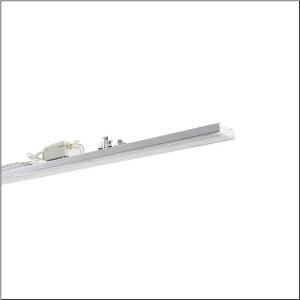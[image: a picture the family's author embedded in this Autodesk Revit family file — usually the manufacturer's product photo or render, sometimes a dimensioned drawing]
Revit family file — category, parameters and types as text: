
# Revit family: licross_11_recessed_ho_51tl12cn4c5m
name_source: partatom
category: Lighting Fixtures
units: mm (PartAtom-declared; Revit-internal decimal feet)

## family parameters
Cut with Voids When Loaded = No
Host = Face
Light Source = No
Part Type = Normal
Room Calculation Point = No
Round Connector Dimension = Use Diameter
Shared = No

## types (1)
- --- (1 x LED, 12740 lm, 66.5 W, 4000K)
    Apparent Load = 67 VA
    CIE Flux Codes = 66 91 98 100 100
    Color Rendering = 80
    Color Temperature = 4000K
    Default Elevation = 1800 mm
    Description = Licross 11 Recessed HO, luminaire insert, of sheet steel, coil coated, white, length: 1.500mm, width: 66mm, height: 67mm, LED rated luminous flux: 12.740lm, light colour: 840, SDCM (Standard Deviation of Colour Matching)MacAdam ≤ 2 SDCM (initial), control gear: ON/OFF Multilumen, CLOi, with plug, 3-pole, with phase selection, mains connection: 220..240V, AC, 50/60Hz, start of lifetime: 67W, end of service life: 75W, internal wiring halogen-free, primary optical cover: cover, of PMMA, light emission: direct distribution, primary light characteristic: symmetric, protection rating (complete): IP40, insulation class (complete): insulation class I (protective earthing), certification: CE, ENEC, VDE, UKCA, protection symbol: D if used in an environment without relevant dust loads with corresponding accessories, impact resistance: IK06, permissible ambient temperature for indoor applications: -35..+35°C, corresponds to IFS (International Featured Standards) requirements for safety and quality in the food industry, reducing of maximum allowable ambient temperature of 5°C with ceiling mounting, LABS conformity tested according to VDMA 24364:2018-05, The light source and the operating device comply with the requirements of the Ecodesign Regulation (EU) 2019/2020 and are replaceable in accordance with this regulation, packaging unit: 1 piece
    Height = 58 mm
    Lamp = 1 x LED
    Lamp Light Flux = 12740 lm
    Lamp Power = 66.5 W
    Lamp count = 1
    Length = 1500 mm
    Luminous efficacy = 192 lm/W
    Manufacturer = Siteco
    ModVariant = No
    Model = 51TL12CN4C5M
    Mounting Place = Ceiling
    Mounting Type = Pendant
    Number of Poles = 1
    OnlyDefault = Yes
    Power Factor = 1
    Product Name = Licross 11 Recessed HO
    Product group = luminaire insert | ceiling pendant
    ProductGroupID = 901
    Protection Class = Protection class I
    Protection Degree = IP 40
    RLX_Detail_Level = 1
    RLX_Emergency_Light_Flux = 0 lm
    RLX_Emergency_Type = 0
    RLX_Emergency_Type_DB = No
    RlxData = <blob elided: 22501 chars, md5=00e9c269>
    Socket = socket
    Standby Power = 0 W
    System Light Flux = 12740 lm
    System Power = 67 W
    Type Comments = factory setting: luminous flux: 100 % | (A | C | E) | 156 mA
    Type Image = l_1296930.jpg
    URL = http://relux.com
    VarID = @adj_000321
    Voltage = 0 V
    Weight = 0.00 kg
    Width = 66 mm

## geometry (parser evidence)
native form markers: Blend x4, Sweep x9
no freeform markers — native parametric forms only
